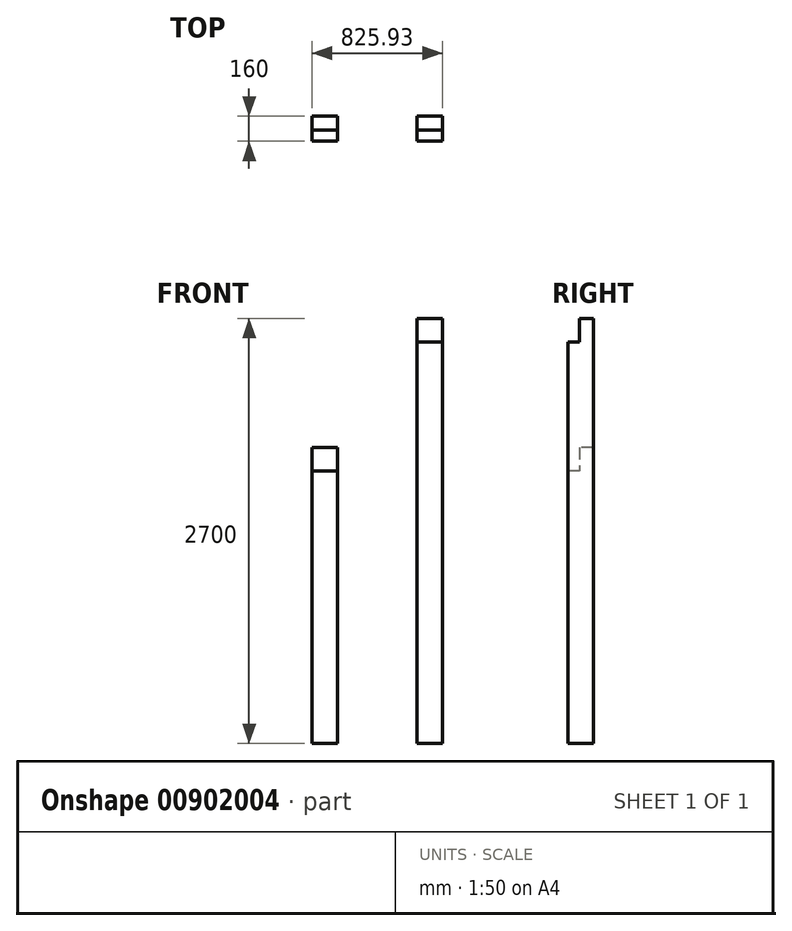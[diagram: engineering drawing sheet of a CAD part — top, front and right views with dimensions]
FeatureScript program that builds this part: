
annotation { "Feature Type Name" : "Feature", "Feature Type Description" : "" }
export const myFeature = defineFeature(function(context is Context, id is Id, definition is map)
    precondition{}
    {
        {
            var Q0;
            Q0=qCreatedBy(makeId("Top.planeOp"),FACE);
            var sketch = newSketch(context, id + "F0", { "sketchPlane" : qUnion([Q0])});
            skLineSegment(sketch, "E0.bottom", {"start": v(80, 80) * mm, "end": v(-80, 80) * mm});
            skLineSegment(sketch, "E0.top", {"start": v(80, -80) * mm, "end": v(-80, -80) * mm});
            skLineSegment(sketch, "E0.left", {"start": v(80, 80) * mm, "end": v(80, -80) * mm});
            skLineSegment(sketch, "E0.right", {"start": v(-80, 80) * mm, "end": v(-80, -80) * mm});
            skPoint(sketch, "E0.middle", {"position": v(0, 0) * mm});
            skSolve(sketch);
        }
        {
            var Q0;
            Q0=makeQuery(id+"F0.imprint","IMPRINT",FACE,{"disambiguationData":[TD([[makeQuery(id+"F0.imprint","IMPRINT",EDGE,{"derivedFrom":sQuery(id+"F0.wireOp",EDGE,"E0.bottom")}),1.0]])]});
            extrude(context, id + "F1", {"entities" : qUnion([Q0]), "depth" : 1880 * mm, "offsetDistance" : 25 * mm});
        }
        {
            var Q0;
            Q0=makeQuery(id+"F1.opExtrude","SWEPT_FACE",FACE,{"disambiguationData":[OSD([sQuery(id+"F0.wireOp",EDGE,"E0.top")])]});
            var sketch = newSketch(context, id + "F2", { "sketchPlane" : qUnion([Q0])});
            skLineSegment(sketch, "E1.bottom", {"start": v(-80, 1880) * mm, "end": v(80, 1880) * mm});
            skLineSegment(sketch, "E1.top", {"start": v(-80, 1730) * mm, "end": v(80, 1730) * mm});
            skLineSegment(sketch, "E1.left", {"start": v(-80, 1880) * mm, "end": v(-80, 1730) * mm});
            skLineSegment(sketch, "E1.right", {"start": v(80, 1880) * mm, "end": v(80, 1730) * mm});
            skSolve(sketch);
        }
        {
            var Q0;
            Q0=makeQuery(id+"F2.imprint","IMPRINT",FACE,{"disambiguationData":[TD([[makeQuery(id+"F2.imprint","IMPRINT",EDGE,{"derivedFrom":sQuery(id+"F2.wireOp",EDGE,"E1.bottom")}),1.0]])]});
            extrude(context, id + "F3", {"entities" : qUnion([Q0]), "operationType" : NewBodyOperationType.REMOVE, "oppositeDirection" : true, "depth" : 70 * mm, "offsetDistance" : 25 * mm});
        }
        {
            var Q0;
            Q0=makeQuery(id+"F1.opExtrude","CAP_FACE",FACE,{"disambiguationData":[OSD([sQuery(id+"F0.wireOp",EDGE,"E0.bottom"),sQuery(id+"F0.wireOp",EDGE,"E0.top"),sQuery(id+"F0.wireOp",EDGE,"E0.left"),sQuery(id+"F0.wireOp",EDGE,"E0.right")])],"isStart":true});
            var sketch = newSketch(context, id + "F4", { "sketchPlane" : qUnion([Q0])});
            skLineSegment(sketch, "E2.bottom", {"start": v(585.93, 80) * mm, "end": v(745.93, 80) * mm});
            skLineSegment(sketch, "E2.top", {"start": v(585.93, -80) * mm, "end": v(745.93, -80) * mm});
            skLineSegment(sketch, "E2.left", {"start": v(585.93, 80) * mm, "end": v(585.93, -80) * mm});
            skLineSegment(sketch, "E2.right", {"start": v(745.93, 80) * mm, "end": v(745.93, -80) * mm});
            skSolve(sketch);
        }
        {
            var Q0;
            Q0 = qSketchRegion(id + "F4", true);
            extrude(context, id + "F5", {"entities" : qUnion([Q0]), "oppositeDirection" : true, "depth" : 2700 * mm, "offsetDistance" : 25 * mm});
        }
        {
            var Q0;
            Q0=makeQuery(id+"F5.opExtrude","SWEPT_FACE",FACE,{"disambiguationData":[OSD([sQuery(id+"F4.wireOp",EDGE,"E2.bottom")])]});
            var sketch = newSketch(context, id + "F6", { "sketchPlane" : qUnion([Q0])});
            skLineSegment(sketch, "E3.bottom", {"start": v(585.93, 2700) * mm, "end": v(745.93, 2700) * mm});
            skLineSegment(sketch, "E3.top", {"start": v(585.93, 2550) * mm, "end": v(745.93, 2550) * mm});
            skLineSegment(sketch, "E3.left", {"start": v(585.93, 2700) * mm, "end": v(585.93, 2550) * mm});
            skLineSegment(sketch, "E3.right", {"start": v(745.93, 2700) * mm, "end": v(745.93, 2550) * mm});
            skSolve(sketch);
        }
        {
            var Q0;
            Q0=makeQuery(id+"F6.imprint","IMPRINT",FACE,{"disambiguationData":[TD([[makeQuery(id+"F6.imprint","IMPRINT",EDGE,{"derivedFrom":sQuery(id+"F6.wireOp",EDGE,"E3.bottom")}),-1.0]])]});
            extrude(context, id + "F7", {"entities" : qUnion([Q0]), "operationType" : NewBodyOperationType.REMOVE, "oppositeDirection" : true, "depth" : 70 * mm, "offsetDistance" : 25 * mm});
        }
    });
